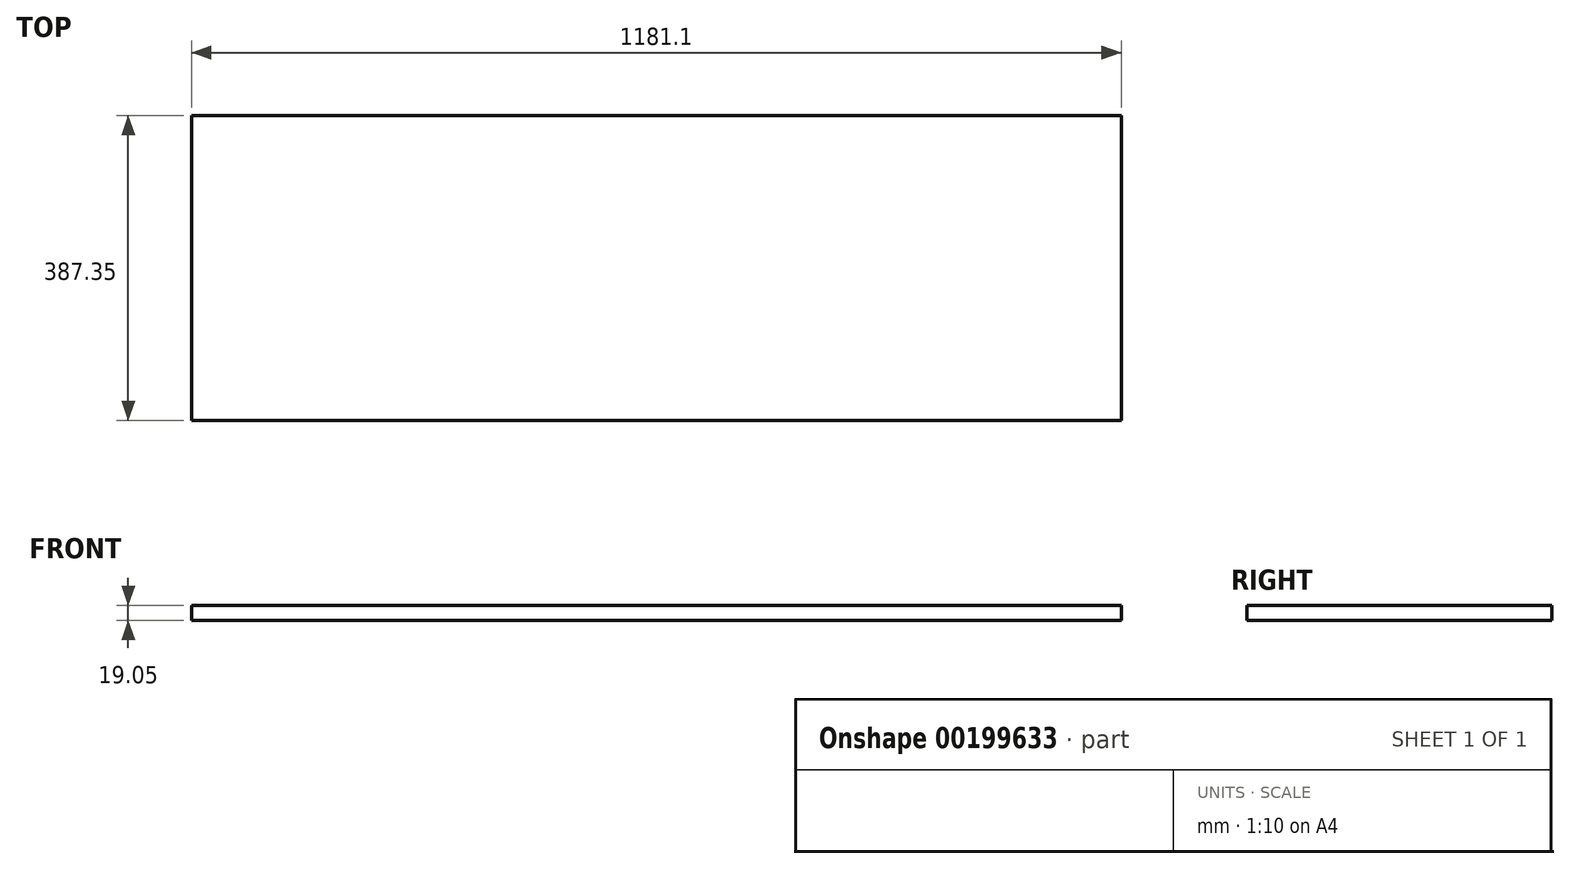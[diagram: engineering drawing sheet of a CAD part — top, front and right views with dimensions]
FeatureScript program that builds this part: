
annotation { "Feature Type Name" : "Feature", "Feature Type Description" : "" }
export const myFeature = defineFeature(function(context is Context, id is Id, definition is map)
    precondition{}
    {
        {
            var Q0;
            Q0=qCreatedBy(makeId("Top.planeOp"),FACE);
            var sketch = newSketch(context, id + "F0", { "sketchPlane" : qUnion([Q0])});
            skLineSegment(sketch, "E0.bottom", {"start": v(-596.75, 66.2) * mm, "end": v(584.35, 66.2) * mm});
            skLineSegment(sketch, "E0.top", {"start": v(-596.75, -321.15) * mm, "end": v(584.35, -321.15) * mm});
            skLineSegment(sketch, "E0.left", {"start": v(-596.75, 66.2) * mm, "end": v(-596.75, -321.15) * mm});
            skLineSegment(sketch, "E0.right", {"start": v(584.35, 66.2) * mm, "end": v(584.35, -321.15) * mm});
            skSolve(sketch);
        }
        {
            var Q0;
            Q0 = qSketchRegion(id + "F0", true);
            extrude(context, id + "F1", {"entities" : qUnion([Q0]), "depth" : 19.05 * mm});
        }
    });
